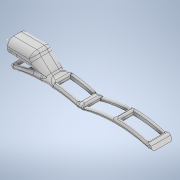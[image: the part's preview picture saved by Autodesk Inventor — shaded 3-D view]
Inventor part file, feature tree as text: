
AUTODESK INVENTOR PART (.ipt)
format: ipt  version: 2022 (Build 260153000, 153)  size: 1,077,760 bytes
history: native  units: in
note: dims shown in document units (in); Inventor stores cm internally (conversion verified against a paired STEP export)
features: fillet x12, sketch x10, extrude x7, plane x2, projected_geometry x2, hole x1
ambient origin geometry x8: Origin, YZ Plane, XZ Plane, XY Plane, X Axis, Y Axis, Z Axis, Center Point
bodies: Solid1 (feature_tree)
feature tree (34):
  extrude  "Extrusion1"  Depth=0.8125in
  hole  "Hole1"  [1 undecoded]
  extrude  "Extrusion2"  Depth=0.125in
  sketch  "Sketch4"  dims[d5=0.8125in d6=0.75in d7=0.375in d8=0.25in d9=0.5635in d10=2.0625in d11=0.0in d15=0.125in]
  sketch  "Sketch5"  dims[d16=0.25in d17=0.25in]
  extrude  "Extrusion3"  Depth=0.25in
  sketch  "Sketch6"  dims[d18=0.5in d19=0.5in]
  extrude  "Extrusion4"  Depth=0.5in
  extrude  "Extrusion5"  TaperAngle=90.0deg  [1 undecoded]
  sketch  "Sketch7"  dims[d20=5.875in d21=0.0in d22=90.0deg d23=0.1969in d24=0.1969in d25=10.0in d26=0.1969in d27=0.1969in]
  sketch  "Sketch8"  dims[d28=1.2025in d29=5.0in d30=0.5in]
  fillet  "Fillet1"  Radius=0.1969in
  fillet  "Fillet2"  Radius=0.1969in
  fillet  "Fillet3"  Radius=10.0in
  fillet  "Fillet4"  Radius=0.1969in
  fillet  "Fillet5"  Radius=0.1969in
  plane  "Work Plane1"
  extrude  "Extrusion6"  Depth=5.0in
  fillet  "Fillet6"  Radius=0.5in
  plane  "Work Plane2"
  extrude  "Extrusion7"  Depth=0.25in
  fillet  "Fillet7"  Radius=5.875in
  fillet  "Fillet8"  Radius=5.875in
  fillet  "Fillet9"  Radius=5.875in
  fillet  "Fillet10"  Radius=0.1181in
  sketch  "Sketch11"  dims[d43=0.25in d44=0.15in d45=2.1875in d46=0.0in d47=0.15in d48=-0.0787in d49=1.15in d50=2.1875in d51=0.0in d52=0.15in d53=0.1in d54=0.1in d55=0.1in d56=0.05in d57=0.125in d12=0.75in d13=0.8108in d14=0.0625in d58=0.0in d59=0.0in d60=0.0in]
  fillet  "Fillet11"  Radius=0.5in
  fillet  "Fillet12"  Radius=0.5in
  sketch  "Sketch1"  dims[d0=12.0in d1=0.8125in]
  sketch  "Sketch2"  dims[d2=2.75in d3=1.625in d4=0.0in]
  projected_geometry  "Projected Loop1"
  projected_geometry  "Projected Loop2"
  sketch  "Sketch9"  dims[d31=0.5in d32=0.25in d33=5.875in d34=0.0in d35=5.875in d36=0.0in d37=5.875in d38=0.0in d39=0.1181in d40=0.5in d41=0.5in]
  sketch  "Sketch10"  dims[d42=0.5in]
note: 2 required parameter values undecoded (feature->parameter linkage not recoverable at this tier; creation-order binding heuristic only, values carry confidence <= 0.55)
